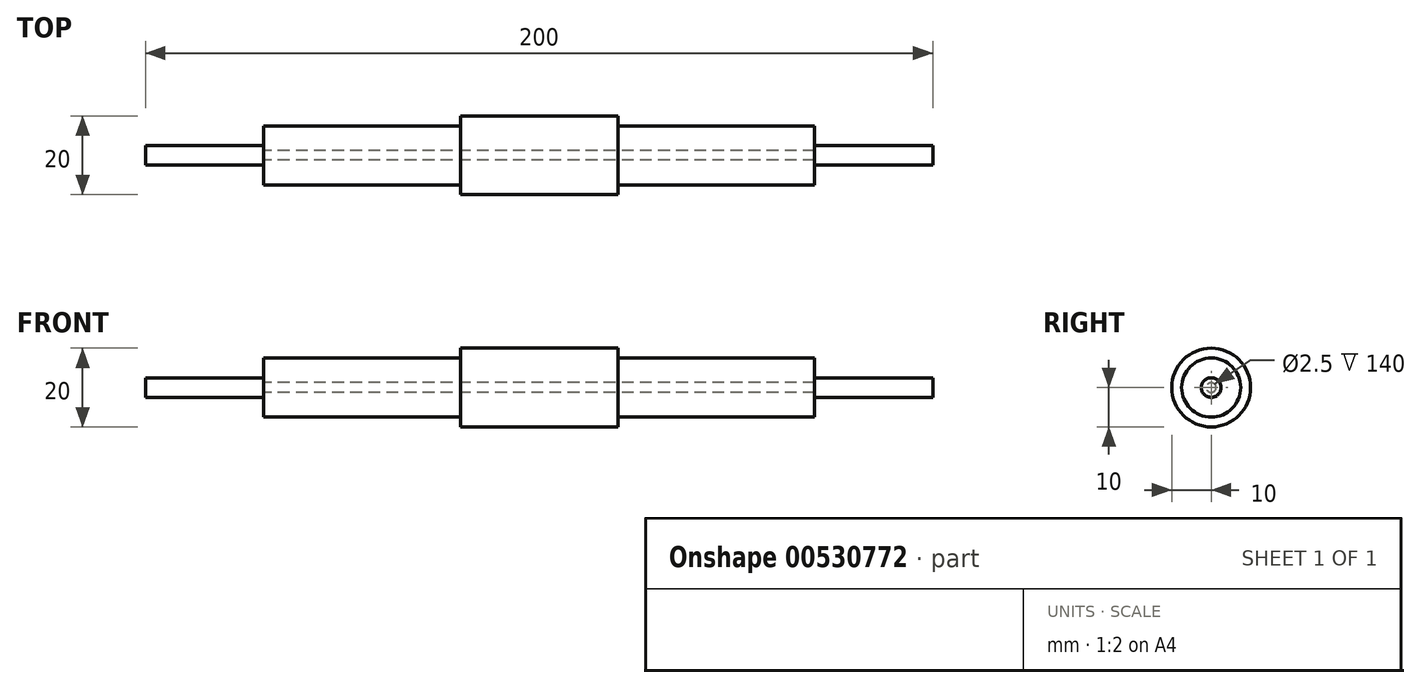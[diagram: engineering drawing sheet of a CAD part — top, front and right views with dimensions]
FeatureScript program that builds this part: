
annotation { "Feature Type Name" : "Feature", "Feature Type Description" : "" }
export const myFeature = defineFeature(function(context is Context, id is Id, definition is map)
    precondition{}
    {
        {
            var Q0;
            Q0=qCreatedBy(makeId("Top.planeOp"),FACE);
            var sketch = newSketch(context, id + "F0", { "sketchPlane" : qUnion([Q0])});
            skLineSegment(sketch, "E0.bottom", {"start": v(0, 0) * mm, "end": v(100, 0) * mm});
            skLineSegment(sketch, "E0.top", {"start": v(0, 2.5) * mm, "end": v(100, 2.5) * mm});
            skLineSegment(sketch, "E0.left", {"start": v(0, 0) * mm, "end": v(0, 2.5) * mm});
            skLineSegment(sketch, "E0.right", {"start": v(100, 0) * mm, "end": v(100, 2.5) * mm});
            skLineSegment(sketch, "E1", {"start": v(-131.16, 0) * mm, "end": v(188.94, 0) * mm, "construction": true});
            skLineSegment(sketch, "E2.bottom", {"start": v(0, 10) * mm, "end": v(20, 10) * mm});
            skLineSegment(sketch, "E2.top", {"start": v(0, 0) * mm, "end": v(20, 0) * mm});
            skLineSegment(sketch, "E2.left", {"start": v(0, 10) * mm, "end": v(0, 0) * mm});
            skLineSegment(sketch, "E2.right", {"start": v(20, 10) * mm, "end": v(20, 0) * mm});
            skLineSegment(sketch, "E3.bottom", {"start": v(20, 7.5) * mm, "end": v(70, 7.5) * mm});
            skLineSegment(sketch, "E3.top", {"start": v(20, 0) * mm, "end": v(70, 0) * mm});
            skLineSegment(sketch, "E3.left", {"start": v(20, 7.5) * mm, "end": v(20, 0) * mm});
            skLineSegment(sketch, "E3.right", {"start": v(70, 7.5) * mm, "end": v(70, 0) * mm});
            skLineSegment(sketch, "E4.bottom", {"start": v(100, 1.25) * mm, "end": v(0, 1.25) * mm});
            skLineSegment(sketch, "E4.top", {"start": v(100, 0) * mm, "end": v(0, 0) * mm});
            skLineSegment(sketch, "E4.left", {"start": v(100, 1.25) * mm, "end": v(100, 0) * mm});
            skLineSegment(sketch, "E4.right", {"start": v(0, 1.25) * mm, "end": v(0, 0) * mm});
            skSolve(sketch);
        }
        {
            var Q0;
            {var subQ5=sQuery(id+"F0.wireOp",EDGE,"E3.bottom");Q0=makeQuery(id+"F0.imprint","IMPRINT",FACE,{"disambiguationData":[TD([[makeQuery(id+"F0.imprint","IMPRINT",EDGE,{"derivedFrom":subQ5}),-1.0]])]});}
            var Q1;
            {var subQ1=sQuery(id+"F0.wireOp",EDGE,"E2.bottom");Q1=makeQuery(id+"F0.imprint","IMPRINT",FACE,{"disambiguationData":[TD([[makeQuery(id+"F0.imprint","IMPRINT",EDGE,{"derivedFrom":subQ1}),-1.0]])]});}
            var Q2;
            {var subQ0=sQuery(id+"F0.wireOp",EDGE,"E0.right");Q2=makeQuery(id+"F0.imprint","IMPRINT",FACE,{"disambiguationData":[TD([[makeQuery(id+"F0.imprint","IMPRINT",EDGE,{"derivedFrom":subQ0}),1.0]])]});}
            var Q3;
            {var subQ0=sQuery(id+"F0.wireOp",EDGE,"E3.right");var subQ1=sQuery(id+"F0.wireOp",EDGE,"E0.top");var subQ2=makeQuery(id+"F0.imprint","INTERSECT",VERTEX,{"derivedFrom":[subQ1,subQ0]});Q3=makeQuery(id+"F0.imprint","IMPRINT",FACE,{"disambiguationData":[TD([[makeQuery(id+"F0.imprint","IMPRINT",EDGE,{"disambiguationData":[TD([[subQ2,1.0]])],"derivedFrom":subQ1}),-1.0]])]});}
            var Q4;
            {var subQ0=sQuery(id+"F0.wireOp",EDGE,"E2.left");var subQ1=sQuery(id+"F0.wireOp",EDGE,"E0.top");var subQ2=makeQuery(id+"F0.imprint","INTERSECT",VERTEX,{"derivedFrom":[subQ1,subQ0]});Q4=makeQuery(id+"F0.imprint","IMPRINT",FACE,{"disambiguationData":[TD([[makeQuery(id+"F0.imprint","IMPRINT",EDGE,{"disambiguationData":[TD([[subQ2,-1.0]])],"derivedFrom":subQ1}),-1.0]])]});}
            var Q5;
            Q5=sQuery(id+"F0.wireOp",EDGE,"E1");
            revolve(context, id + "F1", {"entities" : qUnion([Q0, Q1, Q2, Q3, Q4]), "axis" : qUnion([Q5]), "revolveType" : RevolveType.FULL});
        }
        {
            var Q0;
            Q0=makeQuery(id+"F1.opRevolve","SWEPT_BODY",BODY,{"disambiguationData":[OSD([sQuery(id+"F0.wireOp",EDGE,"E0.top"),sQuery(id+"F0.wireOp",EDGE,"E0.right"),sQuery(id+"F0.wireOp",EDGE,"E2.bottom"),sQuery(id+"F0.wireOp",EDGE,"E2.left"),sQuery(id+"F0.wireOp",EDGE,"E2.right"),sQuery(id+"F0.wireOp",EDGE,"E3.bottom"),sQuery(id+"F0.wireOp",EDGE,"E3.right"),sQuery(id+"F0.wireOp",EDGE,"E4.bottom")])]});
            var Q1;
            Q1=makeQuery(id+"F1.opRevolve","SWEPT_FACE",FACE,{"disambiguationData":[OSD([sQuery(id+"F0.wireOp",EDGE,"E2.left")])]});
            mirror(context, id + "F2", {"operationType" : NewBodyOperationType.ADD, "entities" : qUnion([Q0]), "mirrorPlane" : qUnion([Q1])});
        }
    });
